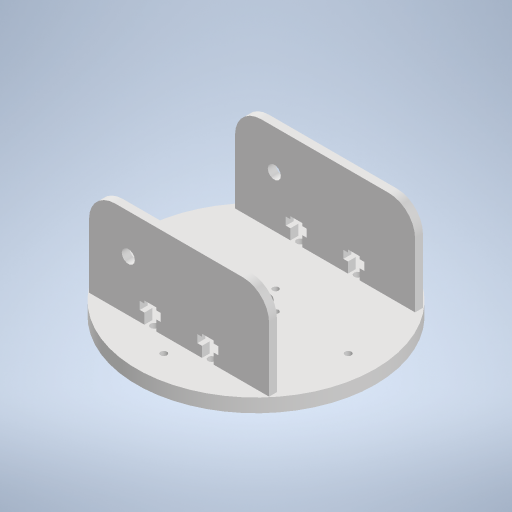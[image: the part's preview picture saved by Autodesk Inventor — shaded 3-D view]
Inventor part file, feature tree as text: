
AUTODESK INVENTOR PART (.ipt)
format: ipt  version: 2023 (Build 270158000, 158)  size: 421,888 bytes
history: native  units: mm
features: extrude x10, sketch x10, pattern_circular x2, mirror x2, other x1, fillet x1
ambient origin geometry x8: Origin, YZ Plane, XZ Plane, XY Plane, X Axis, Y Axis, Z Axis, Center Point
bodies: Body1 (feature_tree)
feature tree (26):
  other  "Sólido1"
  extrude  "Extrusión1"  Depth=5.2mm TaperAngle=0.0deg
  extrude  "Extrusión2"  Depth=2.46mm
  pattern_circular  "Patrón circular1"  Count=4 Angle=360.0deg
  extrude  "Extrusión3"  Depth=11.0mm
  extrude  "Extrusión4"  Depth=7.2mm
  extrude  "Extrusión5"  Depth=2.8mm
  fillet  "Empalme1"  Radius=2.8mm
  extrude  "Extrusión6"  Depth=68.8mm
  mirror  "Simetría1"
  mirror  "Simetría2"
  extrude  "Extrusión7"  Depth=34.5mm TaperAngle=0.0deg
  extrude  "Extrusión8"  Depth=10.0mm
  pattern_circular  "Patrón circular2"  [2 undecoded]
  extrude  "Extrusión9"  Depth=10.0mm
  extrude  "Extrusión10"  Depth=10.0mm
  sketch  "Boceto1"  dims[d0=91.1mm d1=5.2mm d2=0.0mm]
  sketch  "Boceto2"  dims[d3=70.5mm d4=2.46mm]
  sketch  "Boceto3"  dims[d5=5.2mm d6=0.0mm d7=40.0mm d8=360.0deg]
  sketch  "Boceto4"  dims[d11=27.9mm d12=11.0mm]
  sketch  "Boceto5"  dims[d13=7.2mm d14=7.2mm]
  sketch  "Boceto6"  dims[d15=2.6mm d16=0.0mm d17=2.8mm d18=2.8mm]
  sketch  "Boceto7"  dims[d19=2.6mm d20=0.0mm d21=68.8mm]
  sketch  "Boceto8"  dims[d22=3.0mm d23=34.5mm d24=0.0mm]
  sketch  "Boceto9"  dims[d25=10.0mm d26=8.0mm]
  sketch  "Boceto10"  dims[d27=4.5mm d28=3.0mm d29=7.0mm d30=8.0mm d31=34.5mm d32=0.0mm d33=4.5mm d34=9.7mm d35=10.0mm d36=0.0mm d37=15.0mm d38=2.3mm d39=10.0mm d40=0.0mm d41=40.0mm d42=360.0deg d44=0.5mm d45=0.0mm d46=5.0mm d47=15.0mm d48=15.0mm d49=10.0mm d50=0.0mm]
note: 2 required parameter values undecoded (feature->parameter linkage not recoverable at this tier; creation-order binding heuristic only, values carry confidence <= 0.55)
